# Revit family: Double-Uneven
name_source: partatom
category: Doors
revit_build: Autodesk Revit Architecture 2012 (Build: 20110210_1515)
units: mm (PartAtom-declared; Revit-internal decimal feet)

## types (6) — shared parameters
Assembly Code = C1020
Door Material = Door - Panel
Door Thickness = 0' - 2"
Frame Material = Door - Frame
Function = Interior
Thickness = 0' - 2"
Trim Projection Ext = 0' - 1"
Trim Projection Int = 0' - 1"
Trim Width = 0' - 3"
Wall Closure = By host

## per-type parameters (varying)
| type | Height | Width | Width Large Panel | Width Small Panel |
| 52" x 84" | 7' - 0" | 4' - 4" | 3' - 4" | 1' - 0" |
| 54" x 80" | 6' - 8" | 4' - 6" | 3' - 4" | 1' - 2" |
| 54" x 84" | 7' - 0" | 4' - 6" | 3' - 4" | 1' - 2" |
| 48" x 80" | 6' - 8" | 4' - 0" | 2' - 6" | 1' - 6" |
| 44" x 80" | 6' - 8" | 3' - 8" | 2' - 6" | 1' - 2" |
| 50" x 84" | 7' - 0" | 4' - 2" | 3' - 4" | 0' - 10" |

## geometry (parser evidence)
native form markers: Sweep x1
no freeform markers — native parametric forms only
